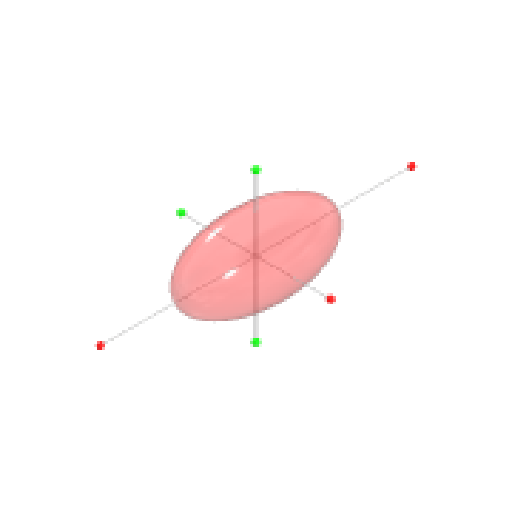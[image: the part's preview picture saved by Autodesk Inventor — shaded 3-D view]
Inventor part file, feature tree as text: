
AUTODESK INVENTOR PART (.ipt)
format: ipt  version: 2023 (Build 270158000, 158)  size: 267,776 bytes
history: native  units: in
note: dims shown in document units (in); Inventor stores cm internally (conversion verified against a paired STEP export)
features: sketch x7, revolve x4, extrude x3, mirror x1, projected_geometry x1
ambient origin geometry x8: Origin, YZ Plane, XZ Plane, XY Plane, X Axis, Y Axis, Z Axis, Center Point
bodies: Solid1 (feature_tree), Solid2 (feature_tree), Solid3 (feature_tree), Solid4 (feature_tree)
feature tree (16):
  revolve  "Revolution1"  [1 undecoded]
  extrude  "Extrusion1"  Depth=1.0in TaperAngle=0.0deg
  mirror  "Mirror1"
  extrude  "Extrusion2"  Depth=1.0in TaperAngle=0.0deg
  extrude  "Extrusion3"  Depth=47.2441in
  revolve  "Revolution2"  [1 undecoded]
  revolve  "Revolution3"  Angle=360.0deg
  revolve  "Revolution4"  [1 undecoded]
  sketch  "Sketch1"  dims[d0=23.622in d1=49.2126in]
  sketch  "Sketch2"  dims[d2=90.0deg d3=1.0in d4=0.0in]
  projected_geometry  "Projected Loop1"
  sketch  "Sketch3"  dims[d5=1.0in d6=0.0in d7=1.0in d8=0.0in]
  sketch  "Sketch4"  dims[d9=47.2441in d10=47.2441in]
  sketch  "Sketch5"  dims[d11=0.25in d12=4.0in]
  sketch  "Sketch6"  dims[d13=4.0in d14=360.0deg]
  sketch  "Sketch7"  dims[d15=98.4252in d16=98.4252in d17=0.25in d18=4.0in d19=4.0in d20=90.0deg d21=47.2441in d22=47.2441in d23=4.0in d24=4.0in d25=0.5in d26=90.0deg d27=0.25in d28=0.25in]
note: 3 required parameter values undecoded (feature->parameter linkage not recoverable at this tier; creation-order binding heuristic only, values carry confidence <= 0.55)
